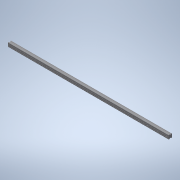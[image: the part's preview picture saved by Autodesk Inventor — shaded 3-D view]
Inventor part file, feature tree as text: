
AUTODESK INVENTOR PART (.ipt)
format: ipt  version: 2022 (Build 260153000, 153)  size: 162,304 bytes
history: native  units: mm (DEFAULTED — no unit token found)
features: other x21, sketch x2, extrude x1, hole x1, pattern_linear x1
ambient origin geometry x8: Origin, YZ Plane, XZ Plane, XY Plane, X Axis, Y Axis, Z Axis, Center Point
bodies: Solid1 (feature_tree)
feature tree (26):
  extrude  "Extrusion1"  Depth=10.0mm TaperAngle=0.0deg
  hole  "Hole1"  [1 undecoded]
  pattern_linear  "Rectangular Pattern1"  [2 undecoded]
  other  "4dummy_XY"
  other  "4dummy_YZ"
  other  "4dummy_ZX"
  other  "4dummy_X"
  other  "4dummy_Y"
  other  "4dummy_Z"
  other  "4dummy_Center"
  other  "4slide_XY"
  other  "4slide_YZ"
  other  "4slide_ZX"
  other  "4slide_X"
  other  "4slide_Y"
  other  "4slide_Z"
  other  "4slide_Center"
  other  "4track_XY"
  other  "4track_YZ"
  other  "4track_ZX"
  other  "4track_X"
  other  "4track_Y"
  other  "4track_Z"
  other  "4track_Center"
  sketch  "Sketch_18"  dims[d2=9.0mm d3=6.0mm d4=14.0mm d5=12.0mm d6=90.0deg d7=29.0mm d8=0.0mm d9=40.0mm d11=80.0mm d12=10.0mm d14=0.0mm d15=0.0mm]
  sketch  "Sketch2"  dims[d0=1371.6mm d1=0.0mm]
note: 3 required parameter values undecoded (feature->parameter linkage not recoverable at this tier; creation-order binding heuristic only, values carry confidence <= 0.55)
